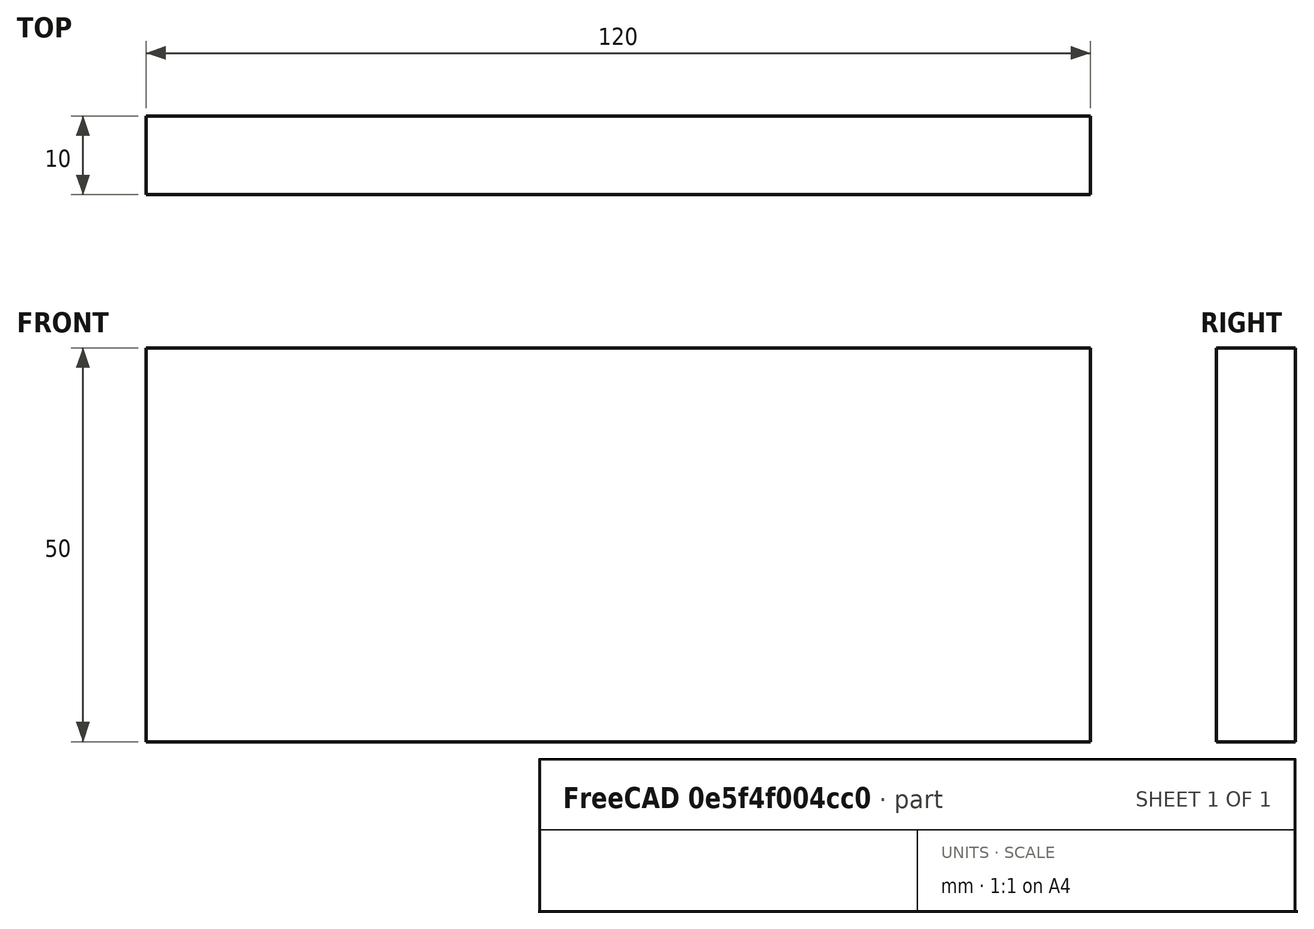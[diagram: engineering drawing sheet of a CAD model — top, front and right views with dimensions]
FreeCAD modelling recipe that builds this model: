
FCSTD DOCUMENT  (FreeCAD 0.15R4671 (Git))
Label: Flat Bar 120x10 EN10058 S235JR
License: All rights reserved
LicenseURL: http://en.wikipedia.org/wiki/All_rights_reserved
objects: Sketcher::SketchObject×1, Part::Extrusion×1
note: 2 computed .brp shape members not serialized (recipe doc carries the construction recipe); baked Part::Feature solids carry a one-line shape summary decoded from their .brp

FEATURE [Sketcher::SketchObject] Sketch
  sketch-geometry (4):
    g0: LineSegment StartX=-60 StartY=-5 StartZ=0 EndX=60 EndY=-5 EndZ=0
    g1: LineSegment StartX=60 StartY=-5 StartZ=0 EndX=60 EndY=5 EndZ=0
    g2: LineSegment StartX=60 StartY=5 StartZ=0 EndX=-60 EndY=5 EndZ=0
    g3: LineSegment StartX=-60 StartY=5 StartZ=0 EndX=-60 EndY=-5 EndZ=0
  constraints (12):
    c: Coincident(g0,g1)
    c: Coincident(g1,g2)
    c: Coincident(g2,g3)
    c: Coincident(g3,g0)
    c: Horizontal(g0)
    c: Horizontal(g2)
    c: Vertical(g1)
    c: Vertical(g3)
    c: Symmetric(g1,g2,g-2)
    c: Symmetric(g0,g1,g-1)
    c: DistanceY(g1) = 10
    c: DistanceX(g0) = 120
FEATURE [Part::Extrusion] Extrude  label="Flat Bar 120x10 EN10058 S235JR"
  Base = -> Sketch
  Dir = (0,0,50)
  Solid = true
